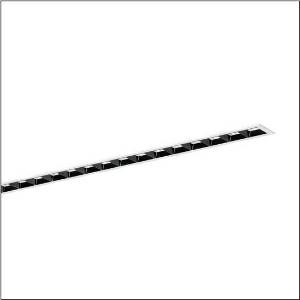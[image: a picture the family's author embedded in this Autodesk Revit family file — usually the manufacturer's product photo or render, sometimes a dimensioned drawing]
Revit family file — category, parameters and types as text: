
# Revit family: silica_21_51mx11db45wb
name_source: partatom
category: Lighting Fixtures
units: mm (PartAtom-declared; Revit-internal decimal feet)

## family parameters
Cut with Voids When Loaded = No
Host = Face
Light Source = No
Part Type = Normal
Room Calculation Point = No
Round Connector Dimension = Use Diameter
Shared = No

## types (1)
- --- (1 x LED, 5400 lm, 32 W, 4000K)
    Apparent Load = 32 VA
    CIE Flux Codes = 87 99 100 100 100
    Color Rendering = 80
    Color Temperature = 4000K
    Default Elevation = 1800 mm
    Description = Silica 21, office luminaire, primary light control with darklight reflector, of PMMA, black, CAT 2 (L<= 3000cd/m²), light emission: direct distribution, primary light characteristic: symmetric, installation type: recessed, LED, rated luminous flux: 5.400lm, luminous efficacy: 169lm/W, light colour: 840, colour temperature: 4000K, control gear: DALI 2, with terminal, 3+2-pole, max. 2.5mm², mains connection: 220..240V, AC, 50/60Hz, rated input power: 32W, luminaire housing, of aluminium, traffic white (RAL 9016), length: 1.528mm, width: 79mm, height: 53mm, protection rating (complete): IP20, insulation class (complete): insulation class I (protective earthing), certification: CE, ENEC, VDE, permissible operating ambient temperature: 0..+35°C, standard: EN 50419, packaging unit: 1 piece
    Height = 0 mm  [stored 0 ft]
    Lamp = 1 x LED
    Lamp Light Flux = 5400 lm
    Lamp Power = 32 W
    Lamp count = 1
    Length = 1527 mm
    Luminous efficacy = 169 lm/W
    Manufacturer = Siteco
    ModVariant = No
    Model = 51MX11DB45WB
    Mounting Place = Ceiling
    Mounting Type = Recessed
    Number of Poles = 1
    OnlyDefault = Yes
    Power Factor = 1
    Product Name = Silica 21
    Product group = office luminaire | ceiling recessed
    ProductGroupID = 400
    Protection Class = Protection class I
    Protection Degree = IP 20
    RLX_Detail_Level = 1
    RLX_Emergency_Light_Flux = 0 lm
    RLX_Emergency_Type = 0
    RLX_Emergency_Type_DB = No
    RlxData = <blob elided: 42337 chars, md5=ed98699a>
    Socket = socket
    Standby Power = 0 W
    System Light Flux = 5400 lm
    System Power = 32 W
    Type Comments = factory setting: luminous flux: 100 % | dim-lin: 254 | 367 mA
    Type Image = l_1335880.jpg
    URL = http://relux.com
    VarID = @adj_123621
    Voltage = 0 V
    Weight = 0.00 kg
    Width = 79 mm

note: [stored X ft] marks values corroborated as IEEE doubles in the binary element streams (Revit-internal decimal feet)

## geometry (parser evidence)
native form markers: Blend x4, Sweep x11
no freeform markers — native parametric forms only
